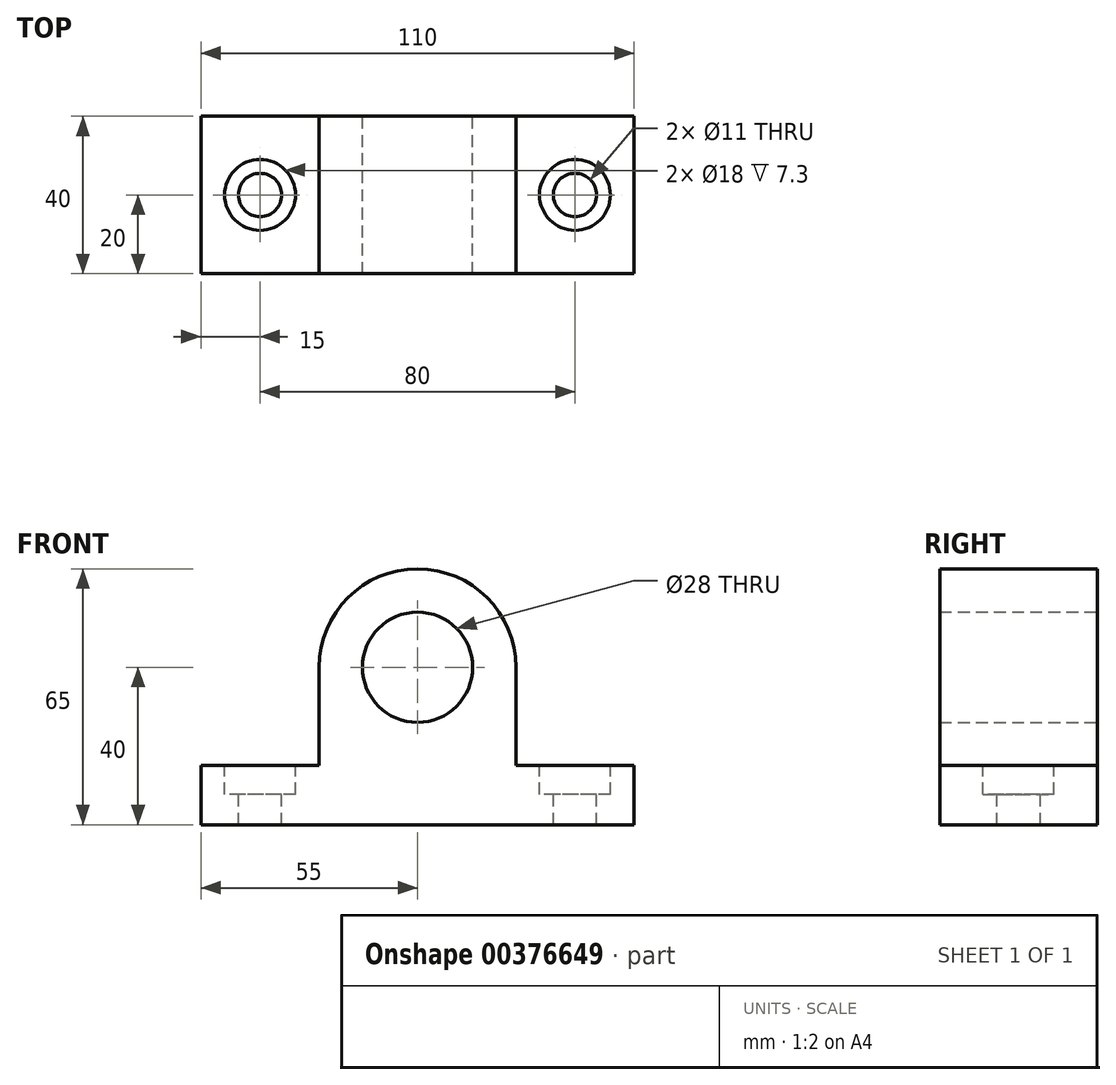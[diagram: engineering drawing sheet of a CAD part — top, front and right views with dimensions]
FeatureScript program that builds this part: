
annotation { "Feature Type Name" : "Feature", "Feature Type Description" : "" }
export const myFeature = defineFeature(function(context is Context, id is Id, definition is map)
    precondition{}
    {
        {
            var Q0;
            Q0=qCreatedBy(makeId("Front.planeOp"),FACE);
            var sketch = newSketch(context, id + "F0", { "sketchPlane" : qUnion([Q0])});
            skLineSegment(sketch, "E0", {"start": v(-55, 0) * mm, "end": v(55, 0) * mm});
            skLineSegment(sketch, "E1", {"start": v(55, 0) * mm, "end": v(55, 15) * mm});
            skLineSegment(sketch, "E2", {"start": v(55, 15) * mm, "end": v(25, 15) * mm});
            skLineSegment(sketch, "E3", {"start": v(25, 15) * mm, "end": v(25, 40) * mm});
            skLineSegment(sketch, "E4", {"start": v(-25, 40) * mm, "end": v(-25, 15) * mm});
            skLineSegment(sketch, "E5", {"start": v(-25, 15) * mm, "end": v(-55, 15) * mm});
            skLineSegment(sketch, "E6", {"start": v(-55, 15) * mm, "end": v(-55, 0) * mm});
            skLineSegment(sketch, "E7", {"start": v(0, 0) * mm, "end": v(0, 40) * mm});
            skArc(sketch, "E8", {"start": v(25, 40) * mm, "mid": v(0, 65) * mm, "end": v(-25, 40) * mm});
            skCircle(sketch, "E9", {"center": v(0, 40) * mm, "radius": 14 * mm});
            skSolve(sketch);
        }
        {
            var Q0;
            Q0=qSketchRegion(id+"F0",true);
            extrude(context, id + "F1", {"entities" : qUnion([Q0]), "depth" : 40 * mm});
        }
        {
            var Q0;
            Q0=makeQuery(id+"F1.opExtrude","SWEPT_FACE",FACE,{"disambiguationData":[OSD([sQuery(id+"F0.wireOp",EDGE,"E5")])]});
            var sketch = newSketch(context, id + "F2", { "sketchPlane" : qUnion([Q0])});
            skCircle(sketch, "E10", {"center": v(-40, -20) * mm, "radius": 9 * mm});
            skCircle(sketch, "E11", {"center": v(-40, -20) * mm, "radius": 5.5 * mm});
            skCircle(sketch, "E12", {"center": v(40, -20) * mm, "radius": 9 * mm});
            skCircle(sketch, "E13", {"center": v(40, -20) * mm, "radius": 5.5 * mm});
            skPoint(sketch, "E14.start.orphan", {"position": v(-55, -20) * mm});
            skSolve(sketch);
        }
        {
            var Q0;
            Q0=makeQuery(id+"F2.imprint","IMPRINT",FACE,{"disambiguationData":[TD([[makeQuery(id+"F2.imprint","IMPRINT",EDGE,{"derivedFrom":sQuery(id+"F2.wireOp",EDGE,"E11")}),1.0]])]});
            var Q1;
            Q1=makeQuery(id+"F2.imprint","IMPRINT",FACE,{"disambiguationData":[TD([[makeQuery(id+"F2.imprint","IMPRINT",EDGE,{"derivedFrom":sQuery(id+"F2.wireOp",EDGE,"E13")}),1.0]])]});
            extrude(context, id + "F3", {"entities" : qUnion([Q0, Q1]), "operationType" : NewBodyOperationType.REMOVE, "oppositeDirection" : true, "depth" : 25 * mm});
        }
        {
            var Q0;
            Q0=makeQuery(id+"F2.imprint","IMPRINT",FACE,{"disambiguationData":[TD([[makeQuery(id+"F2.imprint","IMPRINT",EDGE,{"derivedFrom":sQuery(id+"F2.wireOp",EDGE,"E10")}),1.0]])]});
            var Q1;
            Q1=makeQuery(id+"F2.imprint","IMPRINT",FACE,{"disambiguationData":[TD([[makeQuery(id+"F2.imprint","IMPRINT",EDGE,{"derivedFrom":sQuery(id+"F2.wireOp",EDGE,"E12")}),1.0]])]});
            extrude(context, id + "F4", {"entities" : qUnion([Q0, Q1]), "operationType" : NewBodyOperationType.REMOVE, "oppositeDirection" : true, "depth" : 7.3 * mm});
        }
    });
